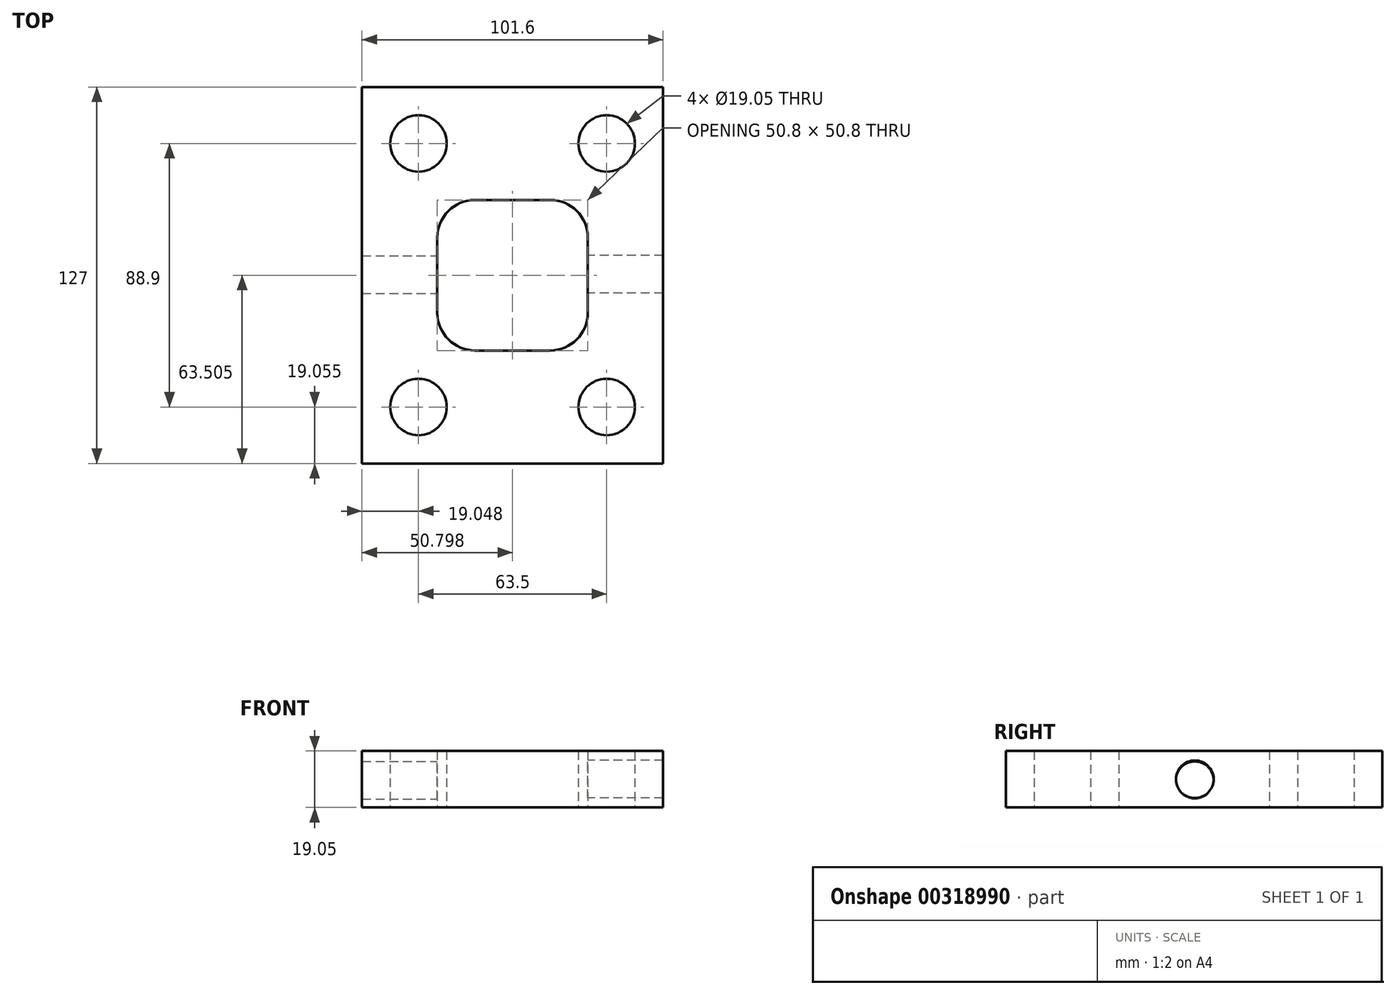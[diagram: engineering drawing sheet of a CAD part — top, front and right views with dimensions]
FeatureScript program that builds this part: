
annotation { "Feature Type Name" : "Feature", "Feature Type Description" : "" }
export const myFeature = defineFeature(function(context is Context, id is Id, definition is map)
    precondition{}
    {
        {
            var Q0;
            Q0=qCreatedBy(makeId("Top.planeOp"),FACE);
            var sketch = newSketch(context, id + "F0", { "sketchPlane" : qUnion([Q0])});
            skLineSegment(sketch, "E0", {"start": v(-61.47, 55.67) * mm, "end": v(-61.47, -71.33) * mm});
            skLineSegment(sketch, "E1", {"start": v(-61.47, 55.67) * mm, "end": v(40.13, 55.67) * mm});
            skLineSegment(sketch, "E2", {"start": v(-61.47, -71.33) * mm, "end": v(40.13, -71.33) * mm});
            skLineSegment(sketch, "E3", {"start": v(40.13, 55.67) * mm, "end": v(40.13, -71.33) * mm});
            skLineSegment(sketch, "E4", {"start": v(-36.07, 4.87) * mm, "end": v(-36.07, -20.53) * mm});
            skLineSegment(sketch, "E5", {"start": v(-23.37, 17.57) * mm, "end": v(2.03, 17.57) * mm});
            skLineSegment(sketch, "E6", {"start": v(14.73, 4.87) * mm, "end": v(14.73, -20.53) * mm});
            skLineSegment(sketch, "E7", {"start": v(-23.37, -33.23) * mm, "end": v(2.03, -33.23) * mm});
            skPoint(sketch, "E8.visualSharp", {"position": v(-36.07, 17.57) * mm});
            skArc(sketch, "E8.filletArc", {"start": v(-23.37, 17.57) * mm, "mid": v(-32.35, 13.86) * mm, "end": v(-36.07, 4.87) * mm});
            skPoint(sketch, "E9.visualSharp", {"position": v(14.73, 17.57) * mm});
            skArc(sketch, "E9.filletArc", {"start": v(14.73, 4.87) * mm, "mid": v(11, 13.86) * mm, "end": v(2.03, 17.57) * mm});
            skPoint(sketch, "E10.visualSharp", {"position": v(14.73, -33.23) * mm});
            skArc(sketch, "E10.filletArc", {"start": v(2.03, -33.23) * mm, "mid": v(11, -29.5) * mm, "end": v(14.73, -20.53) * mm});
            skPoint(sketch, "E11.visualSharp", {"position": v(-36.07, -33.23) * mm});
            skArc(sketch, "E11.filletArc", {"start": v(-36.07, -20.53) * mm, "mid": v(-32.35, -29.5) * mm, "end": v(-23.37, -33.23) * mm});
            skLineSegment(sketch, "E12", {"start": v(-61.47, 55.67) * mm, "end": v(-61.47, 36.62) * mm});
            skCircle(sketch, "E13", {"center": v(-42.42, 36.62) * mm, "radius": 9.53 * mm});
            skCircle(sketch, "E14.MirrorC", {"center": v(21.08, 36.62) * mm, "radius": 9.53 * mm});
            skCircle(sketch, "E15.MirrorC", {"center": v(-42.42, -52.28) * mm, "radius": 9.53 * mm});
            skCircle(sketch, "E16.MirrorC", {"center": v(21.08, -52.28) * mm, "radius": 9.53 * mm});
            skSolve(sketch);
        }
        {
            var Q0;
            Q0=makeQuery(id+"F0.imprint","IMPRINT",FACE,{"disambiguationData":[TD([[makeQuery(id+"F0.imprint","IMPRINT",EDGE,{"derivedFrom":sQuery(id+"F0.wireOp",EDGE,"E0")}),1.0]])]});
            extrude(context, id + "F1", {"entities" : qUnion([Q0]), "depth" : 19.05 * mm});
        }
        {
            var Q0;
            Q0=qCreatedBy(makeId("Right.planeOp"),FACE);
            var sketch = newSketch(context, id + "F2", { "sketchPlane" : qUnion([Q0])});
            skLineSegment(sketch, "E17", {"start": v(-71.06, 19.05) * mm, "end": v(-71.06, 0) * mm});
            skLineSegment(sketch, "E18", {"start": v(-71.06, 0) * mm, "end": v(55.94, 0) * mm});
            skLineSegment(sketch, "E19", {"start": v(55.94, 0) * mm, "end": v(55.94, 19.05) * mm});
            skLineSegment(sketch, "E20", {"start": v(55.94, 19.05) * mm, "end": v(-71.06, 19.05) * mm});
            skPoint(sketch, "E21.endSnap0", {"position": v(-71.06, 9.53) * mm});
            skPoint(sketch, "E22", {"position": v(-7.56, 9.53) * mm});
            skSolve(sketch);
        }
        {
            var Q0;
            Q0=sQuery(id+"F2.wireOp",VERTEX,"E22");
            var Q1;
            Q1=makeQuery(id+"F1.opExtrude","SWEPT_BODY",BODY,{"disambiguationData":[OSD([sQuery(id+"F0.wireOp",EDGE,"E0"),sQuery(id+"F0.wireOp",EDGE,"E1"),sQuery(id+"F0.wireOp",EDGE,"E2"),sQuery(id+"F0.wireOp",EDGE,"E3"),sQuery(id+"F0.wireOp",EDGE,"E4"),sQuery(id+"F0.wireOp",EDGE,"E5"),sQuery(id+"F0.wireOp",EDGE,"E6"),sQuery(id+"F0.wireOp",EDGE,"E7"),sQuery(id+"F0.wireOp",EDGE,"E8.filletArc"),sQuery(id+"F0.wireOp",EDGE,"E9.filletArc"),sQuery(id+"F0.wireOp",EDGE,"E10.filletArc"),sQuery(id+"F0.wireOp",EDGE,"E11.filletArc"),sQuery(id+"F0.wireOp",EDGE,"E12"),sQuery(id+"F0.wireOp",EDGE,"E13"),sQuery(id+"F0.wireOp",EDGE,"E14.MirrorC"),sQuery(id+"F0.wireOp",EDGE,"E15.MirrorC"),sQuery(id+"F0.wireOp",EDGE,"E16.MirrorC")])]});
            hole(context, id + "F3", {"style" : HoleStyle.SIMPLE, "endStyle" : HoleEndStyle.BLIND, "oppositeDirection" : true, "holeDiameter" : 12.7 * mm, "holeDepth" : 127 * mm, "tappedDepth" : 12.7 * mm, "tapClearance" : 3, "locations" : qUnion([Q0]), "scope" : qUnion([Q1])});
        }
        {
            var Q0;
            Q0=qCreatedBy(makeId("Right.planeOp"),FACE);
            var sketch = newSketch(context, id + "F4", { "sketchPlane" : qUnion([Q0])});
            skPoint(sketch, "E23", {"position": v(-7.57, 9.18) * mm});
            skSolve(sketch);
        }
        {
            var Q0;
            Q0=sQuery(id+"F4.wireOp",VERTEX,"E23");
            var Q1;
            Q1=makeQuery(id+"F1.opExtrude","SWEPT_BODY",BODY,{"disambiguationData":[OSD([sQuery(id+"F0.wireOp",EDGE,"E0"),sQuery(id+"F0.wireOp",EDGE,"E1"),sQuery(id+"F0.wireOp",EDGE,"E2"),sQuery(id+"F0.wireOp",EDGE,"E3"),sQuery(id+"F0.wireOp",EDGE,"E4"),sQuery(id+"F0.wireOp",EDGE,"E5"),sQuery(id+"F0.wireOp",EDGE,"E6"),sQuery(id+"F0.wireOp",EDGE,"E7"),sQuery(id+"F0.wireOp",EDGE,"E8.filletArc"),sQuery(id+"F0.wireOp",EDGE,"E9.filletArc"),sQuery(id+"F0.wireOp",EDGE,"E10.filletArc"),sQuery(id+"F0.wireOp",EDGE,"E11.filletArc"),sQuery(id+"F0.wireOp",EDGE,"E12"),sQuery(id+"F0.wireOp",EDGE,"E13"),sQuery(id+"F0.wireOp",EDGE,"E14.MirrorC"),sQuery(id+"F0.wireOp",EDGE,"E15.MirrorC"),sQuery(id+"F0.wireOp",EDGE,"E16.MirrorC")])]});
            hole(context, id + "F5", {"style" : HoleStyle.SIMPLE, "endStyle" : HoleEndStyle.THROUGH, "holeDiameter" : 12.7 * mm, "tappedDepth" : 12.7 * mm, "tapClearance" : 3, "locations" : qUnion([Q0]), "scope" : qUnion([Q1])});
        }
    });
